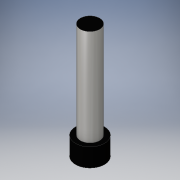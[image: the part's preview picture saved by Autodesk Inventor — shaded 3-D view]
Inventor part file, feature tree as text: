
AUTODESK INVENTOR PART (.ipt)
format: ipt  version: 2016 (Build 200138000, 138)  size: 101,376 bytes
history: native  units: in
note: dims shown in document units (in); Inventor stores cm internally (conversion verified against a paired STEP export)
features: extrude x2, sketch x2
ambient origin geometry x8: Origin, YZ Plane, XZ Plane, XY Plane, X Axis, Y Axis, Z Axis, Center Point
bodies: Solid1 (feature_tree)
feature tree (4):
  extrude  "Extrusion1"  Depth=0.1496in TaperAngle=0.0deg
  extrude  "Extrusion2"  Depth=0.7874in TaperAngle=0.0deg
  sketch  "Sketch1"  dims[d0=0.2362in d1=0.1496in d2=0.0in]
  sketch  "Sketch2"  dims[d3=0.1575in d4=0.7874in d5=0.0in]
